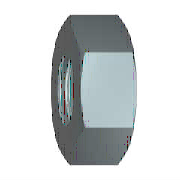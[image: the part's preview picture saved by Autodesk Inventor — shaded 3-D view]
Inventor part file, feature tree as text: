
AUTODESK INVENTOR PART (.ipt)
format: ipt  version: 2022.1 (Build 261234000, 234)  size: 164,864 bytes
history: native  units: mm (DEFAULTED — no unit token found)
features: sketch x3, extrude x1, chamfer x1, hole x1, other x1, plane x1
ambient origin geometry x7: Origin, YZ Plane, XZ Plane, X Axis, Y Axis, Z Axis, Center Point
bodies: Solid1 (feature_tree)
feature tree (8):
  extrude  "Cuerpo"  Depth=2.4mm
  chamfer  "Chaflán1"  Angle=30.0deg  [1 undecoded]
  hole  "Rosca"  [1 undecoded]
  other  "Work Axis1"
  plane  "Work Plane1"
  sketch  "Boceto1"  dims[d0=6.350853mm d1=2.4mm]
  sketch  "Boceto2"  dims[d2=0.0mm]
  sketch  "Boceto3"  dims[d3=30.0deg d4=30.0deg d5=4.6mm d6=4.6mm d7=90.0deg d25=2.459mm d26=6.0mm d27=4.0mm d28=2.0mm d29=14.3117mm d30=8.0mm d31=20.594885mm d8=0.270633mm d9=30.0deg d10=0.270633mm d11=30.0deg d13=0.0mm d14=0.0mm d39=0.0mm d40=0.270633mm d41=0.270633mm d42=0.0mm]
note: 2 required parameter values undecoded (feature->parameter linkage not recoverable at this tier; creation-order binding heuristic only, values carry confidence <= 0.55)
